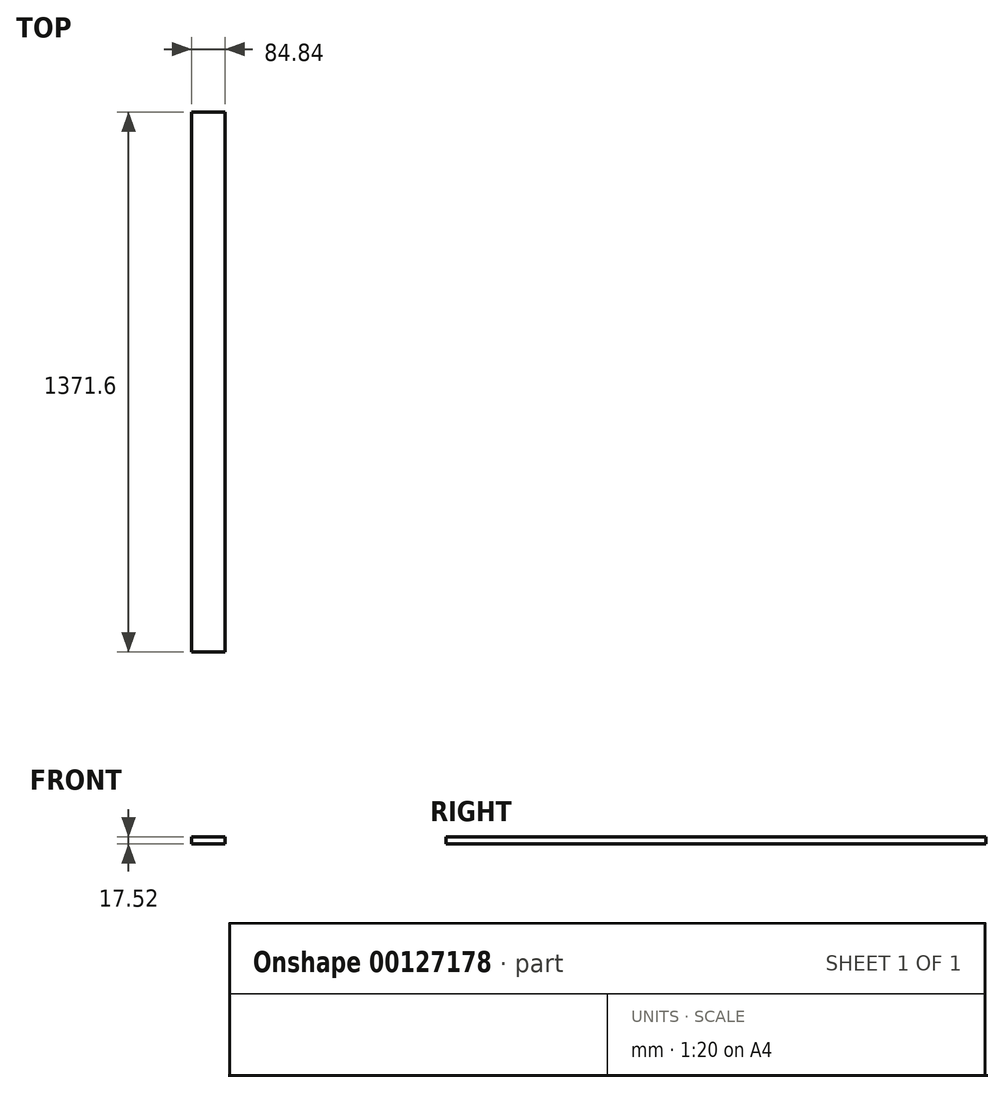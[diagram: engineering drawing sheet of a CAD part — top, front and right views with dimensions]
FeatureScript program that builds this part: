
annotation { "Feature Type Name" : "Feature", "Feature Type Description" : "" }
export const myFeature = defineFeature(function(context is Context, id is Id, definition is map)
    precondition{}
    {
        {
            var Q0;
            Q0=qCreatedBy(makeId("Front.planeOp"),FACE);
            var sketch = newSketch(context, id + "F0", { "sketchPlane" : qUnion([Q0])});
            skLineSegment(sketch, "E0.bottom", {"start": v(42.42, -8.76) * mm, "end": v(-42.42, -8.76) * mm});
            skLineSegment(sketch, "E0.top", {"start": v(42.42, 8.76) * mm, "end": v(-42.42, 8.76) * mm});
            skLineSegment(sketch, "E0.left", {"start": v(42.42, -8.76) * mm, "end": v(42.42, 8.76) * mm});
            skLineSegment(sketch, "E0.right", {"start": v(-42.42, -8.76) * mm, "end": v(-42.42, 8.76) * mm});
            skPoint(sketch, "E0.middle", {"position": v(0, 0) * mm});
            skSolve(sketch);
        }
        {
            var Q0;
            Q0=qSketchRegion(id+"F0",true);
            extrude(context, id + "F1", {"entities" : qUnion([Q0]), "depth" : 1371.6 * mm, "offsetDistance" : 25.4 * mm});
        }
    });
